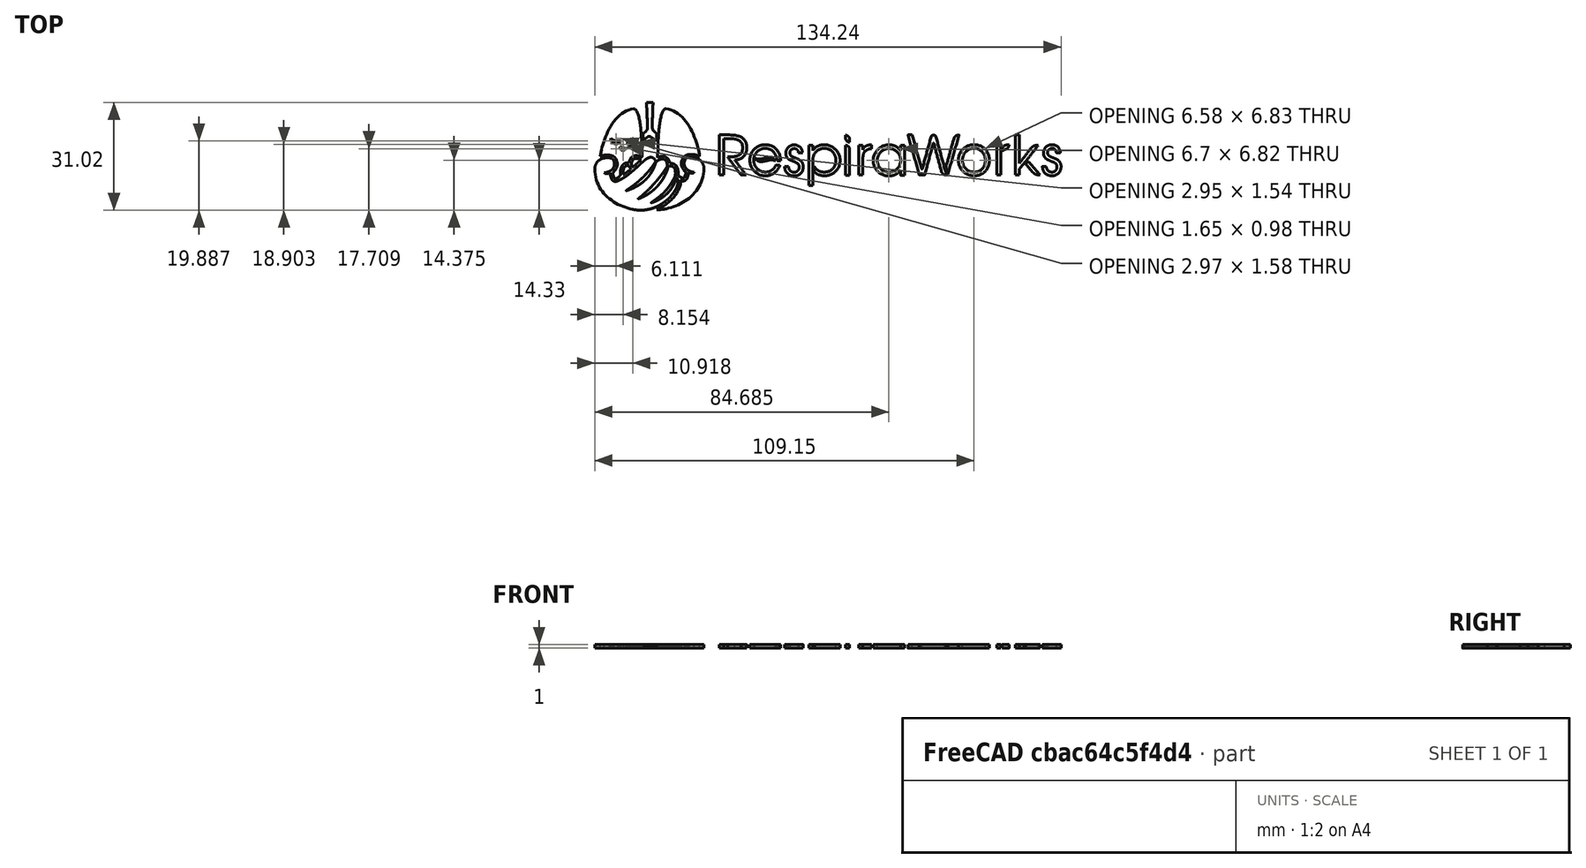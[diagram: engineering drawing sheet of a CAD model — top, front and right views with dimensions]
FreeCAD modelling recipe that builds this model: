
FCSTD DOCUMENT  (FreeCAD 0.18R4 (GitTag))
Label: logo
License: All rights reserved
LicenseURL: http://en.wikipedia.org/wiki/All_rights_reserved
objects: Part::Feature×29, Part::Extrusion×29, Part::MultiFuse×6, Part::Mirroring×2, Part::Cut×1, Part::FeaturePython×1
note: 68 computed .brp shape members not serialized (recipe doc carries the construction recipe); baked Part::Feature solids carry a one-line shape summary decoded from their .brp

FEATURE [Part::Feature] Face  label="LeftLung"
  shape: bbox 12.09 x 20.21 x 2e-07 mm, 1 faces, 0 solids (baked)
FEATURE [Part::Feature] Face001  label="r2-1"
  shape: bbox 1.159 x 8.554 x 2e-07 mm, 1 faces, 0 solids (baked)
FEATURE [Part::Feature] Face002  label="negMouth"
  shape: bbox 1.76 x 1.081 x 2e-07 mm, 1 faces, 0 solids (baked)
FEATURE [Part::Feature] Face003  label="Trachea"
  shape: bbox 4.011 x 10.85 x 2e-07 mm, 1 faces, 0 solids (baked)
FEATURE [Part::Feature] Face004  label="negRightEye"
  shape: bbox 3.134 x 1.688 x 2e-07 mm, 1 faces, 0 solids (baked)
FEATURE [Part::Feature] Face005  label="W-2"
  shape: bbox 3.769 x 11.29 x 2e-07 mm, 1 faces, 0 solids (baked)
FEATURE [Part::Feature] Face006  label="k"
  shape: bbox 6.567 x 11.56 x 2e-07 mm, 1 faces, 0 solids (baked)
FEATURE [Part::Feature] Face007  label="negLeftEye"
  shape: bbox 3.153 x 1.741 x 2e-07 mm, 1 faces, 0 solids (baked)
FEATURE [Part::Feature] Face008  label="LeftHand"
  shape: bbox 23.98 x 15.22 x 2e-07 mm, 1 faces, 0 solids (baked)
FEATURE [Part::Feature] Face009  label="Finger1"
  shape: bbox 2.744 x 2.564 x 2e-07 mm, 1 faces, 0 solids (baked)
FEATURE [Part::Feature] Face010  label="RightLung"
  shape: bbox 12.13 x 20.08 x 2e-07 mm, 1 faces, 0 solids (baked)
FEATURE [Part::Feature] Face011  label="RightHand"
  shape: bbox 13.56 x 15.09 x 2e-07 mm, 1 faces, 0 solids (baked)
FEATURE [Part::Feature] Face012  label="W-1"
  shape: bbox 11.13 x 11.6 x 2e-07 mm, 1 faces, 0 solids (baked)
FEATURE [Part::Feature] Face013  label="Finger2"
  shape: bbox 2.22 x 2.625 x 2e-07 mm, 1 faces, 0 solids (baked)
FEATURE [Part::Feature] Face014  label="k-2"
  shape: bbox 4.239 x 3.757 x 2e-07 mm, 1 faces, 0 solids (baked)
FEATURE [Part::Feature] Face015  label="i-1"
  shape: bbox 1.156 x 1.971 x 2e-07 mm, 1 faces, 0 solids (baked)
FEATURE [Part::Feature] Face016  label="a"
  shape: bbox 9.112 x 9.183 x 2e-07 mm, 1 faces, 0 solids (baked)
FEATURE [Part::Feature] Face017  label="e"
  shape: bbox 9.142 x 9.001 x 2e-07 mm, 1 faces, 0 solids (baked)
FEATURE [Part::Feature] Face018  label="r1"
  shape: bbox 3.58 x 8.758 x 2e-07 mm, 1 faces, 0 solids (baked)
FEATURE [Part::Feature] Face019  label="R"
  shape: bbox 7.842 x 11.56 x 2e-07 mm, 1 faces, 0 solids (baked)
FEATURE [Part::Feature] Face020  label="s"
  shape: bbox 5.342 x 8.932 x 2e-07 mm, 1 faces, 0 solids (baked)
FEATURE [Part::Feature] Face021  label="neg-a"
  shape: bbox 6.699 x 6.927 x 2e-07 mm, 1 faces, 0 solids (baked)
FEATURE [Part::Feature] Face022  label="s2"
  shape: bbox 5.363 x 9.106 x 2e-07 mm, 1 faces, 0 solids (baked)
FEATURE [Part::Feature] Face023  label="i2"
  shape: bbox 1.156 x 8.557 x 2e-07 mm, 1 faces, 0 solids (baked)
FEATURE [Part::Feature] Face024  label="neg-o"
  shape: bbox 6.583 x 6.832 x 2e-07 mm, 1 faces, 0 solids (baked)
FEATURE [Part::Feature] Face025  label="r2-2"
  shape: bbox 1.995 x 1.775 x 2e-07 mm, 1 faces, 0 solids (baked)
FEATURE [Part::Feature] Face026  label="o"
  shape: bbox 8.927 x 8.959 x 2e-07 mm, 1 faces, 0 solids (baked)
FEATURE [Part::Feature] Face027  label="e2"
  shape: bbox 5.94 x 1.154 x 2e-07 mm, 1 faces, 0 solids (baked)
FEATURE [Part::Feature] Face028  label="p"
  shape: bbox 9.051 x 12.05 x 2e-07 mm, 1 faces, 0 solids (baked)
FEATURE [Part::Extrusion] Extrude
  Base = -> Face002
  Dir = (0,0,-1)
  DirMode = 2
  FaceMakerClass = Part::FaceMakerBullseye
  LengthFwd = 1
  LengthRev = 0
  Solid = false
  Symmetric = false
FEATURE [Part::Extrusion] Extrude001
  Base = -> Face004
  Dir = (0,0,-1)
  DirMode = 2
  FaceMakerClass = Part::FaceMakerBullseye
  LengthFwd = 1
  LengthRev = 0
  Solid = false
  Symmetric = false
FEATURE [Part::Extrusion] Extrude002
  Base = -> Face007
  Dir = (0,0,-1)
  DirMode = 2
  FaceMakerClass = Part::FaceMakerBullseye
  LengthFwd = 1
  LengthRev = 0
  Solid = false
  Symmetric = false
FEATURE [Part::Extrusion] Extrude003
  Base = -> Face021
  Dir = (0,0,1)
  DirMode = 2
  FaceMakerClass = Part::FaceMakerBullseye
  LengthFwd = 1
  LengthRev = 0
  Solid = false
  Symmetric = false
FEATURE [Part::Extrusion] Extrude004
  Base = -> Face024
  Dir = (0,0,1)
  DirMode = 2
  FaceMakerClass = Part::FaceMakerBullseye
  LengthFwd = 1
  LengthRev = 0
  Solid = false
  Symmetric = false
FEATURE [Part::MultiFuse] Fusion  label="negDown"
  Shapes = -> [Extrude,Extrude002,Extrude001]
FEATURE [Part::MultiFuse] Fusion001  label="negUp"
  Shapes = -> [Extrude003,Extrude004]
FEATURE [Part::Mirroring] Part__Mirroring  label="negDown (Mirror #1)"
  Base = (0,0,0)
  Normal = (0,0,1)
  Source = -> Fusion
FEATURE [Part::MultiFuse] Fusion002  label="Negative"
  Placement = pos=(-62,255,0) rot=(0,0,1;0rad)
  Shapes = -> [Part__Mirroring,Fusion001]
FEATURE [Part::Extrusion] Extrude005
  Base = -> Face
  Dir = (0,0,1)
  DirMode = 2
  FaceMakerClass = Part::FaceMakerBullseye
  LengthFwd = 1
  LengthRev = 0
  Solid = false
  Symmetric = false
FEATURE [Part::Extrusion] Extrude006
  Base = -> Face001
  Dir = (0,0,1)
  DirMode = 2
  FaceMakerClass = Part::FaceMakerBullseye
  LengthFwd = 1
  LengthRev = 0
  Solid = false
  Symmetric = false
FEATURE [Part::Extrusion] Extrude007
  Base = -> Face003
  Dir = (0,0,1)
  DirMode = 2
  FaceMakerClass = Part::FaceMakerBullseye
  LengthFwd = 1
  LengthRev = 0
  Solid = false
  Symmetric = false
FEATURE [Part::Extrusion] Extrude008
  Base = -> Face005
  Dir = (0,0,1)
  DirMode = 2
  FaceMakerClass = Part::FaceMakerBullseye
  LengthFwd = 1
  LengthRev = 0
  Solid = false
  Symmetric = false
FEATURE [Part::Extrusion] Extrude009
  Base = -> Face006
  Dir = (0,0,1)
  DirMode = 2
  FaceMakerClass = Part::FaceMakerBullseye
  LengthFwd = 1
  LengthRev = 0
  Solid = false
  Symmetric = false
FEATURE [Part::Extrusion] Extrude010
  Base = -> Face008
  Dir = (0,0,-1)
  DirMode = 2
  FaceMakerClass = Part::FaceMakerBullseye
  LengthFwd = 1
  LengthRev = 0
  Solid = false
  Symmetric = false
FEATURE [Part::Extrusion] Extrude011
  Base = -> Face009
  Dir = (0,0,-1)
  DirMode = 2
  FaceMakerClass = Part::FaceMakerBullseye
  LengthFwd = 1
  LengthRev = 0
  Solid = false
  Symmetric = false
FEATURE [Part::Extrusion] Extrude012
  Base = -> Face010
  Dir = (0,0,-1)
  DirMode = 2
  FaceMakerClass = Part::FaceMakerBullseye
  LengthFwd = 1
  LengthRev = 0
  Solid = false
  Symmetric = false
FEATURE [Part::Extrusion] Extrude013
  Base = -> Face011
  Dir = (0,0,-1)
  DirMode = 2
  FaceMakerClass = Part::FaceMakerBullseye
  LengthFwd = 1
  LengthRev = 0
  Solid = false
  Symmetric = false
FEATURE [Part::Extrusion] Extrude014
  Base = -> Face012
  Dir = (0,0,1)
  DirMode = 2
  FaceMakerClass = Part::FaceMakerBullseye
  LengthFwd = 1
  LengthRev = 0
  Solid = false
  Symmetric = false
FEATURE [Part::Extrusion] Extrude015
  Base = -> Face013
  Dir = (0,0,-1)
  DirMode = 2
  FaceMakerClass = Part::FaceMakerBullseye
  LengthFwd = 1
  LengthRev = 0
  Solid = false
  Symmetric = false
FEATURE [Part::Extrusion] Extrude016
  Base = -> Face014
  Dir = (0,0,1)
  DirMode = 2
  FaceMakerClass = Part::FaceMakerBullseye
  LengthFwd = 1
  LengthRev = 0
  Solid = false
  Symmetric = false
FEATURE [Part::Extrusion] Extrude017
  Base = -> Face015
  Dir = (0,0,-1)
  DirMode = 2
  FaceMakerClass = Part::FaceMakerBullseye
  LengthFwd = 1
  LengthRev = 0
  Solid = false
  Symmetric = false
FEATURE [Part::Extrusion] Extrude018
  Base = -> Face016
  Dir = (0,0,-1)
  DirMode = 2
  FaceMakerClass = Part::FaceMakerBullseye
  LengthFwd = 1
  LengthRev = 0
  Solid = false
  Symmetric = false
FEATURE [Part::Extrusion] Extrude019
  Base = -> Face017
  Dir = (0,0,1)
  DirMode = 2
  FaceMakerClass = Part::FaceMakerBullseye
  LengthFwd = 1
  LengthRev = 0
  Solid = false
  Symmetric = false
FEATURE [Part::Extrusion] Extrude020
  Base = -> Face018
  Dir = (0,0,-1)
  DirMode = 2
  FaceMakerClass = Part::FaceMakerBullseye
  LengthFwd = 1
  LengthRev = 0
  Solid = false
  Symmetric = false
FEATURE [Part::Extrusion] Extrude021
  Base = -> Face019
  Dir = (0,0,-1)
  DirMode = 2
  FaceMakerClass = Part::FaceMakerBullseye
  LengthFwd = 1
  LengthRev = 0
  Solid = false
  Symmetric = false
FEATURE [Part::Extrusion] Extrude022
  Base = -> Face020
  Dir = (0,0,-1)
  DirMode = 2
  FaceMakerClass = Part::FaceMakerBullseye
  LengthFwd = 1
  LengthRev = 0
  Solid = false
  Symmetric = false
FEATURE [Part::Extrusion] Extrude023
  Base = -> Face022
  Dir = (0,0,-1)
  DirMode = 2
  FaceMakerClass = Part::FaceMakerBullseye
  LengthFwd = 1
  LengthRev = 0
  Solid = false
  Symmetric = false
FEATURE [Part::Extrusion] Extrude024
  Base = -> Face023
  Dir = (0,0,-1)
  DirMode = 2
  FaceMakerClass = Part::FaceMakerBullseye
  LengthFwd = 1
  LengthRev = 0
  Solid = false
  Symmetric = false
FEATURE [Part::Extrusion] Extrude025
  Base = -> Face025
  Dir = (0,0,1)
  DirMode = 2
  FaceMakerClass = Part::FaceMakerBullseye
  LengthFwd = 1
  LengthRev = 0
  Solid = false
  Symmetric = false
FEATURE [Part::Extrusion] Extrude026
  Base = -> Face026
  Dir = (0,0,-1)
  DirMode = 2
  FaceMakerClass = Part::FaceMakerBullseye
  LengthFwd = 1
  LengthRev = 0
  Solid = false
  Symmetric = false
FEATURE [Part::Extrusion] Extrude027
  Base = -> Face027
  Dir = (0,0,-1)
  DirMode = 2
  FaceMakerClass = Part::FaceMakerBullseye
  LengthFwd = 1
  LengthRev = 0
  Solid = false
  Symmetric = false
FEATURE [Part::Extrusion] Extrude028
  Base = -> Face028
  Dir = (0,0,1)
  DirMode = 2
  FaceMakerClass = Part::FaceMakerBullseye
  LengthFwd = 1
  LengthRev = 0
  Solid = false
  Symmetric = false
FEATURE [Part::MultiFuse] Fusion003  label="posUp"
  Shapes = -> [Extrude005,Extrude006,Extrude007,Extrude008,Extrude009,Extrude014,Extrude016,Extrude019,Extrude025,Extrude028]
FEATURE [Part::MultiFuse] Fusion004  label="posDown"
  Shapes = -> [Extrude010,Extrude011,Extrude012,Extrude013,Extrude027,Extrude021,Extrude024,Extrude026,Extrude022,Extrude023,Extrude017,Extrude018,Extrude015,Extrude020]
FEATURE [Part::Mirroring] Part__Mirroring001  label="posDown (Mirror #2)"
  Base = (0,0,0)
  Normal = (0,0,1)
  Source = -> Fusion004
FEATURE [Part::MultiFuse] Fusion005  label="Positive"
  Placement = pos=(-62,255,0) rot=(0,0,1;0rad)
  Shapes = -> [Part__Mirroring001,Fusion003]
FEATURE [Part::Cut] Cut  label="RW-LogoHorizontal-1mm-Extrude"
  Base = -> Fusion005
  Tool = -> Fusion002
FEATURE [Part::FeaturePython] Clone  label="RW-LogoHorizontal-1mm-Extrude001"  # Draft clone (typed FeaturePython)
  AttacherType = Attacher::AttachEngine3D
  Fuse = false
  Objects = -> [Cut]
  Scale = (1,1,1)
